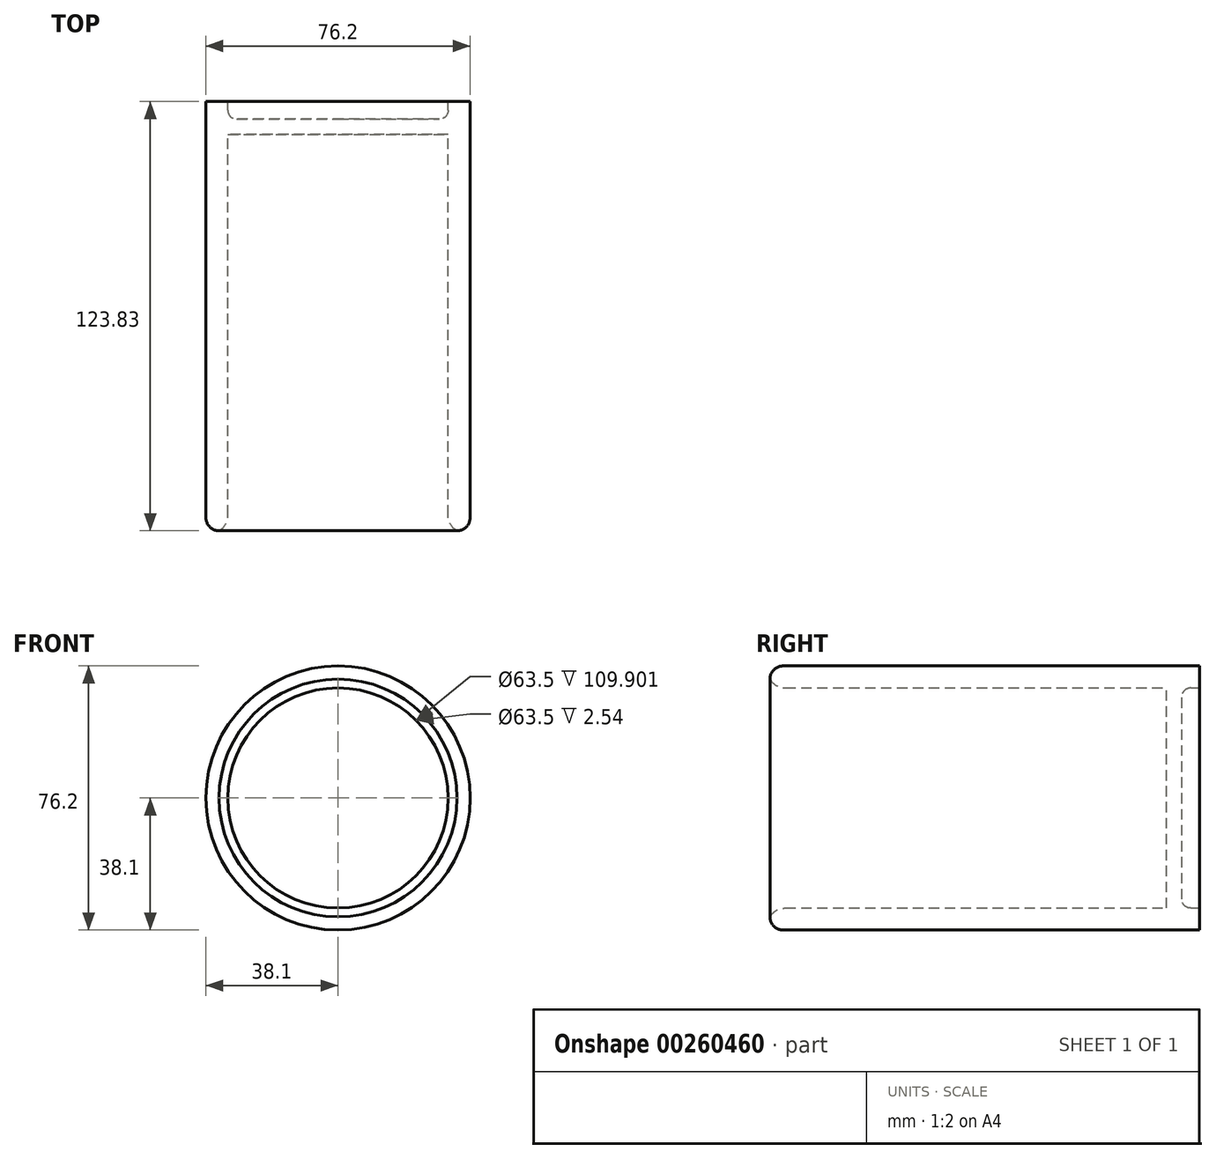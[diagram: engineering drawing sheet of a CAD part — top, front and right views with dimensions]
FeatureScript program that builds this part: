
annotation { "Feature Type Name" : "Feature", "Feature Type Description" : "" }
export const myFeature = defineFeature(function(context is Context, id is Id, definition is map)
    precondition{}
    {
        {
            var Q0;
            Q0=qCreatedBy(makeId("Front.planeOp"),FACE);
            var sketch = newSketch(context, id + "F0", { "sketchPlane" : qUnion([Q0])});
            skCircle(sketch, "E0", {"center": v(0, 0) * mm, "radius": 38.1 * mm});
            skCircle(sketch, "E1", {"center": v(0, 0) * mm, "radius": 31.75 * mm});
            skSolve(sketch);
        }
        {
            var Q0;
            Q0=makeQuery(id+"F0.imprint","IMPRINT",FACE,{"disambiguationData":[TD([[makeQuery(id+"F0.imprint","IMPRINT",EDGE,{"derivedFrom":sQuery(id+"F0.wireOp",EDGE,"E0")}),1.0]])]});
            extrude(context, id + "F1", {"entities" : qUnion([Q0]), "depth" : 123.82 * mm});
        }
        {
            var Q0;
            Q0=makeQuery(id+"F0.imprint","IMPRINT",FACE,{"disambiguationData":[TD([[makeQuery(id+"F0.imprint","IMPRINT",EDGE,{"derivedFrom":sQuery(id+"F0.wireOp",EDGE,"E1")}),1.0]])]});
            extrude(context, id + "F2", {"entities" : qUnion([Q0]), "operationType" : NewBodyOperationType.ADD, "depth" : 9.52 * mm});
        }
        {
            var Q0;
            Q0=makeQuery(id+"F1.opExtrude","CAP_EDGE",EDGE,{"disambiguationData":[OSD([sQuery(id+"F0.wireOp",EDGE,"E0")])],"isStart":false});
            fillet(context, id + "F3", {"entities" : qUnion([Q0]), "radius" : 3.8 * mm, "tangentPropagation" : true, "allowEdgeOverflow" : false});
        }
        {
            var Q0;
            Q0=makeQuery(id+"F1.opExtrude","CAP_EDGE",EDGE,{"disambiguationData":[OSD([sQuery(id+"F0.wireOp",EDGE,"E1")])],"isStart":false});
            fillet(context, id + "F4", {"entities" : qUnion([Q0]), "radius" : 5.08 * mm, "tangentPropagation" : true, "allowEdgeOverflow" : false});
        }
        {
            var Q0;
            Q0=makeQuery(id+"F0.imprint","IMPRINT",FACE,{"disambiguationData":[TD([[makeQuery(id+"F0.imprint","IMPRINT",EDGE,{"derivedFrom":sQuery(id+"F0.wireOp",EDGE,"E1")}),1.0]])]});
            extrude(context, id + "F5", {"entities" : qUnion([Q0]), "operationType" : NewBodyOperationType.REMOVE, "depth" : 5.08 * mm});
        }
        {
            var Q0;
            Q0=makeQuery(id+"F5.boolean.opBoolean","COPY",EDGE,{"derivedFrom":makeQuery(id+"F5.opExtrude","CAP_EDGE",EDGE,{"disambiguationData":[OSD([sQuery(id+"F0.wireOp",EDGE,"E1")])],"isStart":false})});
            var Q1;
            Q1=makeQuery(id+"F5.boolean.opBoolean","COPY",EDGE,{"derivedFrom":makeQuery(id+"F5.opExtrude","CAP_EDGE",EDGE,{"disambiguationData":[OSD([sQuery(id+"F0.wireOp",EDGE,"E1")])],"isStart":true})});
            fillet(context, id + "F6", {"entities" : qUnion([Q0, Q1]), "radius" : 2.54 * mm, "tangentPropagation" : true, "allowEdgeOverflow" : false});
        }
    });
